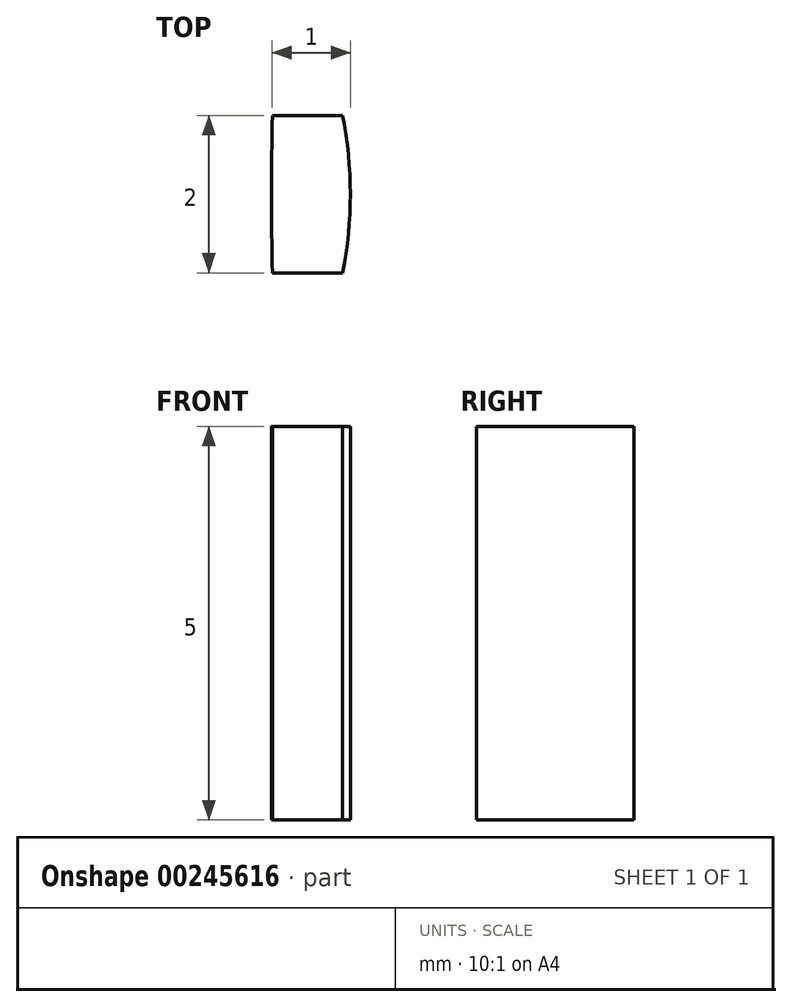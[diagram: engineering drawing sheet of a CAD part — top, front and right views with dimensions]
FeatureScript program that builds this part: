
annotation { "Feature Type Name" : "Feature", "Feature Type Description" : "" }
export const myFeature = defineFeature(function(context is Context, id is Id, definition is map)
    precondition{}
    {
        {
            var Q0;
            Q0=qCreatedBy(makeId("Top.planeOp"),FACE);
            var sketch = newSketch(context, id + "F0", { "sketchPlane" : qUnion([Q0])});
            skArc(sketch, "E0", {"start": v(1, -1) * mm, "mid": v(1.1, 0) * mm, "end": v(1, 1) * mm});
            skPoint(sketch, "E1.endSnap0", {"position": v(1.1, 0) * mm});
            skLineSegment(sketch, "E2", {"start": v(0.1, 1) * mm, "end": v(1, 1) * mm});
            skLineSegment(sketch, "E3", {"start": v(0.1, -1) * mm, "end": v(1, -1) * mm});
            skArc(sketch, "E4", {"start": v(0.1, 1) * mm, "mid": v(0.1, 0) * mm, "end": v(0.1, -1) * mm});
            skSolve(sketch);
        }
        {
            var Q0;
            Q0=makeQuery(id+"F0.imprint","IMPRINT",FACE,{"disambiguationData":[TD([[makeQuery(id+"F0.imprint","IMPRINT",EDGE,{"derivedFrom":sQuery(id+"F0.wireOp",EDGE,"E0")}),1.0]])]});
            extrude(context, id + "F1", {"entities" : qUnion([Q0]), "depth" : 5 * mm});
        }
    });
